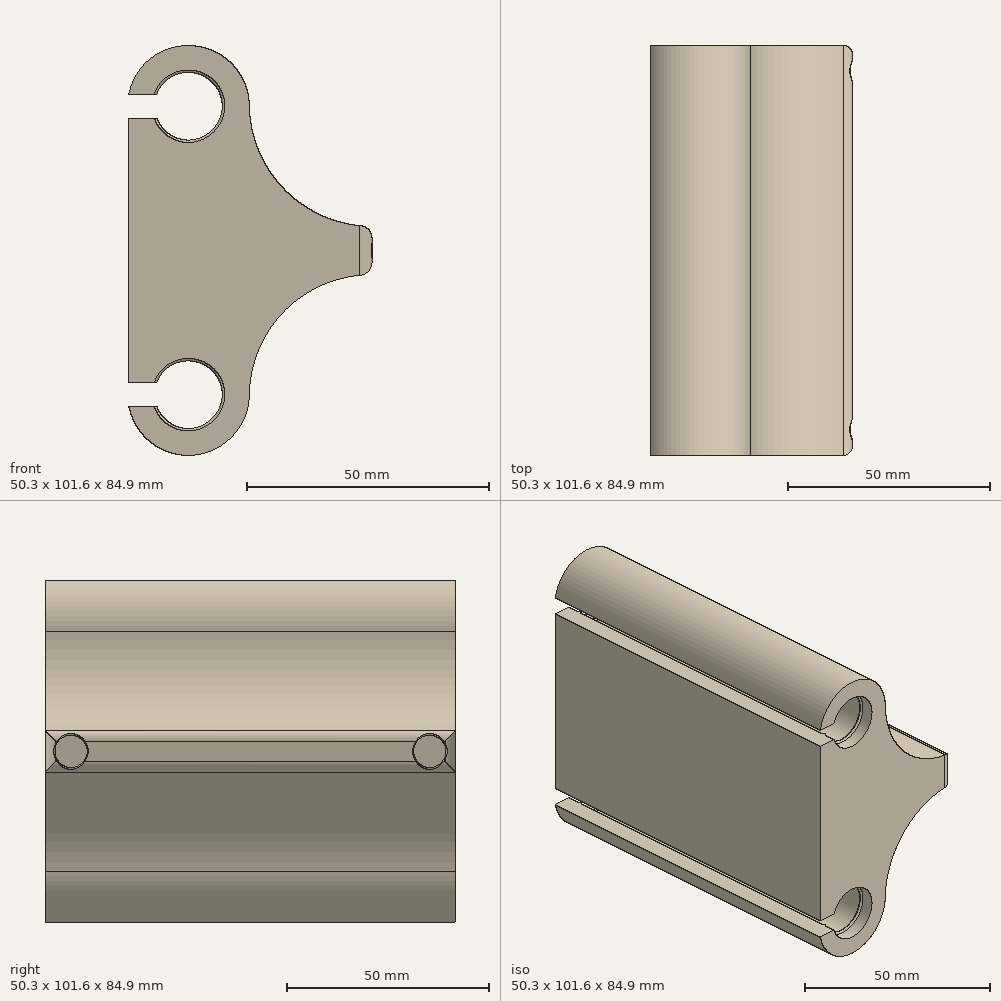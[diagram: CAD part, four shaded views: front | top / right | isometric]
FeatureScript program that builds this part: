
annotation { "Feature Type Name" : "Feature", "Feature Type Description" : "" }
export const myFeature = defineFeature(function(context is Context, id is Id, definition is map)
    precondition{}
    {
        {
            var Q0;
            Q0=qCreatedBy(makeId("Front.planeOp"),FACE);
            var sketch = newSketch(context, id + "F0", { "sketchPlane" : qUnion([Q0])});
            skArc(sketch, "E0", {"start": v(-7.06, 27.3) * mm, "mid": v(7.5, 29.85) * mm, "end": v(-7.06, 32.38) * mm});
            skArc(sketch, "E1", {"start": v(-7.06, -32.38) * mm, "mid": v(7.5, -29.85) * mm, "end": v(-7.06, -27.3) * mm});
            skLineSegment(sketch, "E2", {"start": v(0, 29.85) * mm, "end": v(0, 0) * mm, "construction": true});
            skLineSegment(sketch, "E3", {"start": v(0, 0) * mm, "end": v(0, -29.85) * mm, "construction": true});
            skLineSegment(sketch, "E4", {"start": v(0, 29.85) * mm, "end": v(-12.32, 29.85) * mm, "construction": true});
            skLineSegment(sketch, "E5", {"start": v(-12.32, 27.3) * mm, "end": v(-12.32, -27.3) * mm});
            skLineSegment(sketch, "E6", {"start": v(-12.32, -29.85) * mm, "end": v(0, -29.85) * mm, "construction": true});
            skLineSegment(sketch, "E7", {"start": v(0, 29.85) * mm, "end": v(12.58, 29.85) * mm, "construction": true});
            skLineSegment(sketch, "E8", {"start": v(12.58, -29.85) * mm, "end": v(0, -29.84) * mm, "construction": true});
            skLineSegment(sketch, "E9", {"start": v(37.98, 0) * mm, "end": v(37.98, 5) * mm});
            skLineSegment(sketch, "E10", {"start": v(37.98, 0) * mm, "end": v(37.98, -5) * mm});
            skArc(sketch, "E11", {"start": v(12.58, 29.84) * mm, "mid": v(20.22, 12.24) * mm, "end": v(37.98, 5) * mm});
            skArc(sketch, "E12", {"start": v(37.98, -5) * mm, "mid": v(20.22, -12.24) * mm, "end": v(12.58, -29.85) * mm});
            skLineSegment(sketch, "E13", {"start": v(37.98, -5) * mm, "end": v(12.58, -5) * mm, "construction": true});
            skLineSegment(sketch, "E14", {"start": v(37.98, 5) * mm, "end": v(12.58, 5) * mm, "construction": true});
            skLineSegment(sketch, "E15", {"start": v(-12.32, 27.3) * mm, "end": v(-7.06, 27.3) * mm});
            skLineSegment(sketch, "E16", {"start": v(-7.06, 32.39) * mm, "end": v(-12.32, 32.39) * mm});
            skLineSegment(sketch, "E17", {"start": v(-3.73, 29.85) * mm, "end": v(0, 29.85) * mm, "construction": true});
            skPoint(sketch, "E18.orphan", {"position": v(-12.32, 32.39) * mm});
            skPoint(sketch, "E19.orphan", {"position": v(-3.73, 32.39) * mm});
            skPoint(sketch, "E20.orphan", {"position": v(-3.73, 27.3) * mm});
            skLineSegment(sketch, "E21", {"start": v(-12.32, -29.84) * mm, "end": v(-12.32, -32.39) * mm, "construction": true});
            skLineSegment(sketch, "E22", {"start": v(-3, -32.38) * mm, "end": v(-12.32, -32.39) * mm});
            skLineSegment(sketch, "E23", {"start": v(-3, -32.38) * mm, "end": v(-3, -27.3) * mm, "construction": true});
            skLineSegment(sketch, "E24", {"start": v(-12.32, -27.3) * mm, "end": v(-3, -27.3) * mm});
            skLineSegment(sketch, "E25", {"start": v(-12.32, -27.3) * mm, "end": v(-12.32, -29.84) * mm, "construction": true});
            skLineSegment(sketch, "E26", {"start": v(-12.32, 32.39) * mm, "end": v(-12.32, 27.3) * mm, "construction": true});
            skArc(sketch, "E27", {"start": v(-12.32, -32.39) * mm, "mid": v(1.28, -42.36) * mm, "end": v(12.58, -29.85) * mm});
            skArc(sketch, "E28.trimOffspring", {"start": v(12.58, 29.84) * mm, "mid": v(1.28, 42.36) * mm, "end": v(-12.32, 32.38) * mm});
            skLineSegment(sketch, "E29", {"start": v(12.58, -29.85) * mm, "end": v(0, -29.85) * mm, "construction": true});
            skLineSegment(sketch, "E30", {"start": v(12.58, 29.84) * mm, "end": v(0, 29.84) * mm, "construction": true});
            skLineSegment(sketch, "E31", {"start": v(12.58, 29.85) * mm, "end": v(12.58, -29.85) * mm, "construction": true});
            skSolve(sketch);
        }
        {
            var Q0;
            Q0 = qSketchRegion(id + "F0", true);
            extrude(context, id + "F1", {"entities" : qUnion([Q0]), "endBound" : BoundingType.SYMMETRIC, "depth" : 101.6 * mm});
        }
        {
            var Q0;
            Q0=makeQuery(id+"F1.opExtrude","SWEPT_FACE",FACE,{"disambiguationData":[OSD([sQuery(id+"F0.wireOp",EDGE,"E9"),sQuery(id+"F0.wireOp",EDGE,"E10")])]});
            var sketch = newSketch(context, id + "F2", { "sketchPlane" : qUnion([Q0])});
            skCircle(sketch, "E32", {"center": v(-44.45, 0) * mm, "radius": 4 * mm});
            skCircle(sketch, "E33", {"center": v(44.45, 0) * mm, "radius": 4 * mm});
            skLineSegment(sketch, "E34", {"start": v(44.45, 0) * mm, "end": v(0, 0) * mm, "construction": true});
            skLineSegment(sketch, "E35", {"start": v(0, 0) * mm, "end": v(-44.45, 0) * mm, "construction": true});
            skSolve(sketch);
        }
        {
            var Q0;
            Q0 = qSketchRegion(id + "F2", true);
            extrude(context, id + "F3", {"entities" : qUnion([Q0]), "operationType" : NewBodyOperationType.REMOVE, "oppositeDirection" : true, "depth" : 25.4 * mm});
        }
        {
            var Q0;
            Q0=makeQuery(id+"F1.opExtrude","CAP_EDGE",EDGE,{"disambiguationData":[OSD([sQuery(id+"F0.wireOp",EDGE,"E9"),sQuery(id+"F0.wireOp",EDGE,"E10")])],"isStart":false});
            var Q1;
            Q1=makeQuery(id+"F1.opExtrude","CAP_EDGE",EDGE,{"disambiguationData":[OSD([sQuery(id+"F0.wireOp",EDGE,"E9"),sQuery(id+"F0.wireOp",EDGE,"E10")])],"isStart":true});
            var Q2;
            Q2=makeQuery(id+"F1.opExtrude","SWEPT_EDGE",EDGE,{"disambiguationData":[OSD([sQuery(id+"F0.wireOp",EDGE,"E9"),sQuery(id+"F0.wireOp",EDGE,"E11")])]});
            var Q3;
            Q3=makeQuery(id+"F1.opExtrude","SWEPT_EDGE",EDGE,{"disambiguationData":[OSD([sQuery(id+"F0.wireOp",EDGE,"E10"),sQuery(id+"F0.wireOp",EDGE,"E12")])]});
            fillet(context, id + "F4", {"entities" : qUnion([Q0, Q1, Q2, Q3]), "radius" : 2.54 * mm, "tangentPropagation" : true, "allowEdgeOverflow" : false});
        }
        {
            var Q0;
            Q0=makeQuery(id+"F4.opFillet","BLEND_EDGE",EDGE,{"blendedFrom":[makeQuery(id+"F1.opExtrude","SWEPT_EDGE",EDGE,{"disambiguationData":[OSD([sQuery(id+"F0.wireOp",EDGE,"E9"),sQuery(id+"F0.wireOp",EDGE,"E11")])]}),makeQuery(id+"F3.boolean.opBoolean","COPY",FACE,{"derivedFrom":makeQuery(id+"F3.opExtrude","SWEPT_FACE",FACE,{"disambiguationData":[OSD([sQuery(id+"F2.wireOp",EDGE,"E32")])]})})],"blendedInto":[makeQuery(id+"F3.boolean.opBoolean","COPY",FACE,{"derivedFrom":makeQuery(id+"F3.opExtrude","SWEPT_FACE",FACE,{"disambiguationData":[OSD([sQuery(id+"F2.wireOp",EDGE,"E32")])]})})]});
            var Q1;
            Q1=makeQuery(id+"F3.boolean.opBoolean","COPY",EDGE,{"derivedFrom":makeQuery(id+"F3.opExtrude","CAP_EDGE",EDGE,{"disambiguationData":[OSD([sQuery(id+"F2.wireOp",EDGE,"E32")])],"isStart":true})});
            var Q2;
            Q2=makeQuery(id+"F4.opFillet","BLEND_EDGE",EDGE,{"blendedFrom":[makeQuery(id+"F1.opExtrude","CAP_EDGE",EDGE,{"disambiguationData":[OSD([sQuery(id+"F0.wireOp",EDGE,"E9"),sQuery(id+"F0.wireOp",EDGE,"E10")])],"isStart":false}),makeQuery(id+"F3.boolean.opBoolean","COPY",FACE,{"derivedFrom":makeQuery(id+"F3.opExtrude","SWEPT_FACE",FACE,{"disambiguationData":[OSD([sQuery(id+"F2.wireOp",EDGE,"E32")])]})})],"blendedInto":[makeQuery(id+"F3.boolean.opBoolean","COPY",FACE,{"derivedFrom":makeQuery(id+"F3.opExtrude","SWEPT_FACE",FACE,{"disambiguationData":[OSD([sQuery(id+"F2.wireOp",EDGE,"E32")])]})})]});
            var Q3;
            Q3=makeQuery(id+"F4.opFillet","BLEND_EDGE",EDGE,{"blendedFrom":[makeQuery(id+"F1.opExtrude","SWEPT_EDGE",EDGE,{"disambiguationData":[OSD([sQuery(id+"F0.wireOp",EDGE,"E10"),sQuery(id+"F0.wireOp",EDGE,"E12")])]}),makeQuery(id+"F3.boolean.opBoolean","COPY",FACE,{"derivedFrom":makeQuery(id+"F3.opExtrude","SWEPT_FACE",FACE,{"disambiguationData":[OSD([sQuery(id+"F2.wireOp",EDGE,"E32")])]})})],"blendedInto":[makeQuery(id+"F3.boolean.opBoolean","COPY",FACE,{"derivedFrom":makeQuery(id+"F3.opExtrude","SWEPT_FACE",FACE,{"disambiguationData":[OSD([sQuery(id+"F2.wireOp",EDGE,"E32")])]})})]});
            var Q4;
            Q4=makeQuery(id+"F4.opFillet","BLEND_EDGE",EDGE,{"blendedFrom":[makeQuery(id+"F1.opExtrude","SWEPT_EDGE",EDGE,{"disambiguationData":[OSD([sQuery(id+"F0.wireOp",EDGE,"E9"),sQuery(id+"F0.wireOp",EDGE,"E11")])]}),makeQuery(id+"F3.boolean.opBoolean","COPY",FACE,{"derivedFrom":makeQuery(id+"F3.opExtrude","SWEPT_FACE",FACE,{"disambiguationData":[OSD([sQuery(id+"F2.wireOp",EDGE,"E33")])]})})],"blendedInto":[makeQuery(id+"F3.boolean.opBoolean","COPY",FACE,{"derivedFrom":makeQuery(id+"F3.opExtrude","SWEPT_FACE",FACE,{"disambiguationData":[OSD([sQuery(id+"F2.wireOp",EDGE,"E33")])]})})]});
            fillet(context, id + "F5", {"entities" : qUnion([Q0, Q1, Q2, Q3, Q4]), "radius" : 0.25 * mm, "tangentPropagation" : true, "allowEdgeOverflow" : false});
        }
        {
            var Q0;
            Q0=makeQuery(id+"F1.opExtrude","CAP_FACE",FACE,{"disambiguationData":[OSD([sQuery(id+"F0.wireOp",EDGE,"E0"),sQuery(id+"F0.wireOp",EDGE,"E1"),sQuery(id+"F0.wireOp",EDGE,"Dn6yR88z-cTen-pDva-7UtK-05UkhO3JCPIs"),sQuery(id+"F0.wireOp",EDGE,"qG1Z1W0Z-cVSD-Mn3b-kE61-azpgbx6w5QhA"),sQuery(id+"F0.wireOp",EDGE,"E5"),sQuery(id+"F0.wireOp",EDGE,"E9"),sQuery(id+"F0.wireOp",EDGE,"E10"),sQuery(id+"F0.wireOp",EDGE,"E11"),sQuery(id+"F0.wireOp",EDGE,"E12"),sQuery(id+"F0.wireOp",EDGE,"E15"),sQuery(id+"F0.wireOp",EDGE,"E16"),sQuery(id+"F0.wireOp",EDGE,"E22"),sQuery(id+"F0.wireOp",EDGE,"E24")])],"isStart":false});
            cPlane(context, id + "F6", {"entities" : qUnion([Q0]), "cplaneType" : CPlaneType.OFFSET, "offset" : 3.5 * mm, "oppositeDirection" : true, "width" : 152.4 * mm, "height" : 152.4 * mm});
        }
        {
            var Q0;
            Q0=qCreatedBy(id+"F6.planeOp",FACE);
            var sketch = newSketch(context, id + "F7", { "sketchPlane" : qUnion([Q0])});
            skArc(sketch, "E36", {"start": v(-6.51, 27.3) * mm, "mid": v(7, 29.85) * mm, "end": v(-6.51, 32.38) * mm});
            skArc(sketch, "E37", {"start": v(-7.06, 27.3) * mm, "mid": v(7.5, 29.85) * mm, "end": v(-7.06, 32.38) * mm});
            skLineSegment(sketch, "E38", {"start": v(-7.06, 32.38) * mm, "end": v(-7.06, 32.38) * mm});
            skLineSegment(sketch, "E39", {"start": v(-7.06, 32.38) * mm, "end": v(-7.06, 27.3) * mm, "construction": true});
            skLineSegment(sketch, "E40", {"start": v(-7.06, 27.3) * mm, "end": v(-7.06, 27.3) * mm});
            skLineSegment(sketch, "E41", {"start": v(-6.51, 32.38) * mm, "end": v(-7.06, 32.38) * mm});
            skLineSegment(sketch, "E42", {"start": v(-6.51, 27.3) * mm, "end": v(-7.06, 27.3) * mm});
            skSolve(sketch);
        }
        {
            var Q0;
            Q0 = qSketchRegion(id + "F7", true);
            extrude(context, id + "F8", {"entities" : qUnion([Q0]), "oppositeDirection" : true, "depth" : 1 * mm});
        }
        {
            var Q0;
            Q0=makeQuery(id+"F8.opExtrude","SWEPT_BODY",BODY,{"disambiguationData":[OSD([sQuery(id+"F7.wireOp",EDGE,"E36"),sQuery(id+"F7.wireOp",EDGE,"E37"),sQuery(id+"F7.wireOp",EDGE,"E38"),sQuery(id+"F7.wireOp",EDGE,"E40")])]});
            var Q1;
            Q1=qCreatedBy(makeId("Top.planeOp"),FACE);
            mirror(context, id + "F9", {"entities" : qUnion([Q0]), "mirrorPlane" : qUnion([Q1])});
        }
        {
            var Q0;
            Q0=makeQuery(id+"F9.opPattern","COPY",BODY,{"derivedFrom":makeQuery(id+"F8.opExtrude","SWEPT_BODY",BODY,{"disambiguationData":[OSD([sQuery(id+"F7.wireOp",EDGE,"E36"),sQuery(id+"F7.wireOp",EDGE,"E37"),sQuery(id+"F7.wireOp",EDGE,"E38"),sQuery(id+"F7.wireOp",EDGE,"E40")])]}),"instanceName":"1"});
            var Q1;
            Q1=makeQuery(id+"F8.opExtrude","SWEPT_BODY",BODY,{"disambiguationData":[OSD([sQuery(id+"F7.wireOp",EDGE,"E36"),sQuery(id+"F7.wireOp",EDGE,"E37"),sQuery(id+"F7.wireOp",EDGE,"E38"),sQuery(id+"F7.wireOp",EDGE,"E40")])]});
            var Q2;
            Q2=qCreatedBy(makeId("Front.planeOp"),FACE);
            mirror(context, id + "F10", {"operationType" : NewBodyOperationType.ADD, "entities" : qUnion([Q0, Q1]), "mirrorPlane" : qUnion([Q2])});
        }
        {
            var Q0;
            Q0=makeQuery(id+"F8.opExtrude","CAP_EDGE",EDGE,{"disambiguationData":[OSD([sQuery(id+"F7.wireOp",EDGE,"E36")])],"isStart":true});
            var Q1;
            Q1=makeQuery(id+"F8.opExtrude","CAP_EDGE",EDGE,{"disambiguationData":[OSD([sQuery(id+"F7.wireOp",EDGE,"E36")])],"isStart":false});
            var Q2;
            Q2=makeQuery(id+"F10.opPattern","COPY",EDGE,{"derivedFrom":makeQuery(id+"F8.opExtrude","CAP_EDGE",EDGE,{"disambiguationData":[OSD([sQuery(id+"F7.wireOp",EDGE,"E36")])],"isStart":true}),"instanceName":"1"});
            var Q3;
            Q3=makeQuery(id+"F10.opPattern","COPY",EDGE,{"derivedFrom":makeQuery(id+"F8.opExtrude","CAP_EDGE",EDGE,{"disambiguationData":[OSD([sQuery(id+"F7.wireOp",EDGE,"E36")])],"isStart":false}),"instanceName":"1"});
            var Q4;
            Q4=makeQuery(id+"F10.opPattern","COPY",EDGE,{"derivedFrom":makeQuery(id+"F9.opPattern","COPY",EDGE,{"derivedFrom":makeQuery(id+"F8.opExtrude","CAP_EDGE",EDGE,{"disambiguationData":[OSD([sQuery(id+"F7.wireOp",EDGE,"E36")])],"isStart":true}),"instanceName":"1"}),"instanceName":"1"});
            var Q5;
            Q5=makeQuery(id+"F10.opPattern","COPY",EDGE,{"derivedFrom":makeQuery(id+"F9.opPattern","COPY",EDGE,{"derivedFrom":makeQuery(id+"F8.opExtrude","CAP_EDGE",EDGE,{"disambiguationData":[OSD([sQuery(id+"F7.wireOp",EDGE,"E36")])],"isStart":false}),"instanceName":"1"}),"instanceName":"1"});
            var Q6;
            Q6=makeQuery(id+"F9.opPattern","COPY",EDGE,{"derivedFrom":makeQuery(id+"F8.opExtrude","CAP_EDGE",EDGE,{"disambiguationData":[OSD([sQuery(id+"F7.wireOp",EDGE,"E36")])],"isStart":false}),"instanceName":"1"});
            var Q7;
            Q7=makeQuery(id+"F9.opPattern","COPY",EDGE,{"derivedFrom":makeQuery(id+"F8.opExtrude","CAP_EDGE",EDGE,{"disambiguationData":[OSD([sQuery(id+"F7.wireOp",EDGE,"E36")])],"isStart":true}),"instanceName":"1"});
            fillet(context, id + "F11", {"entities" : qUnion([Q0, Q1, Q2, Q3, Q4, Q5, Q6, Q7]), "radius" : 0.5 * mm, "tangentPropagation" : true, "allowEdgeOverflow" : false});
        }
    });
